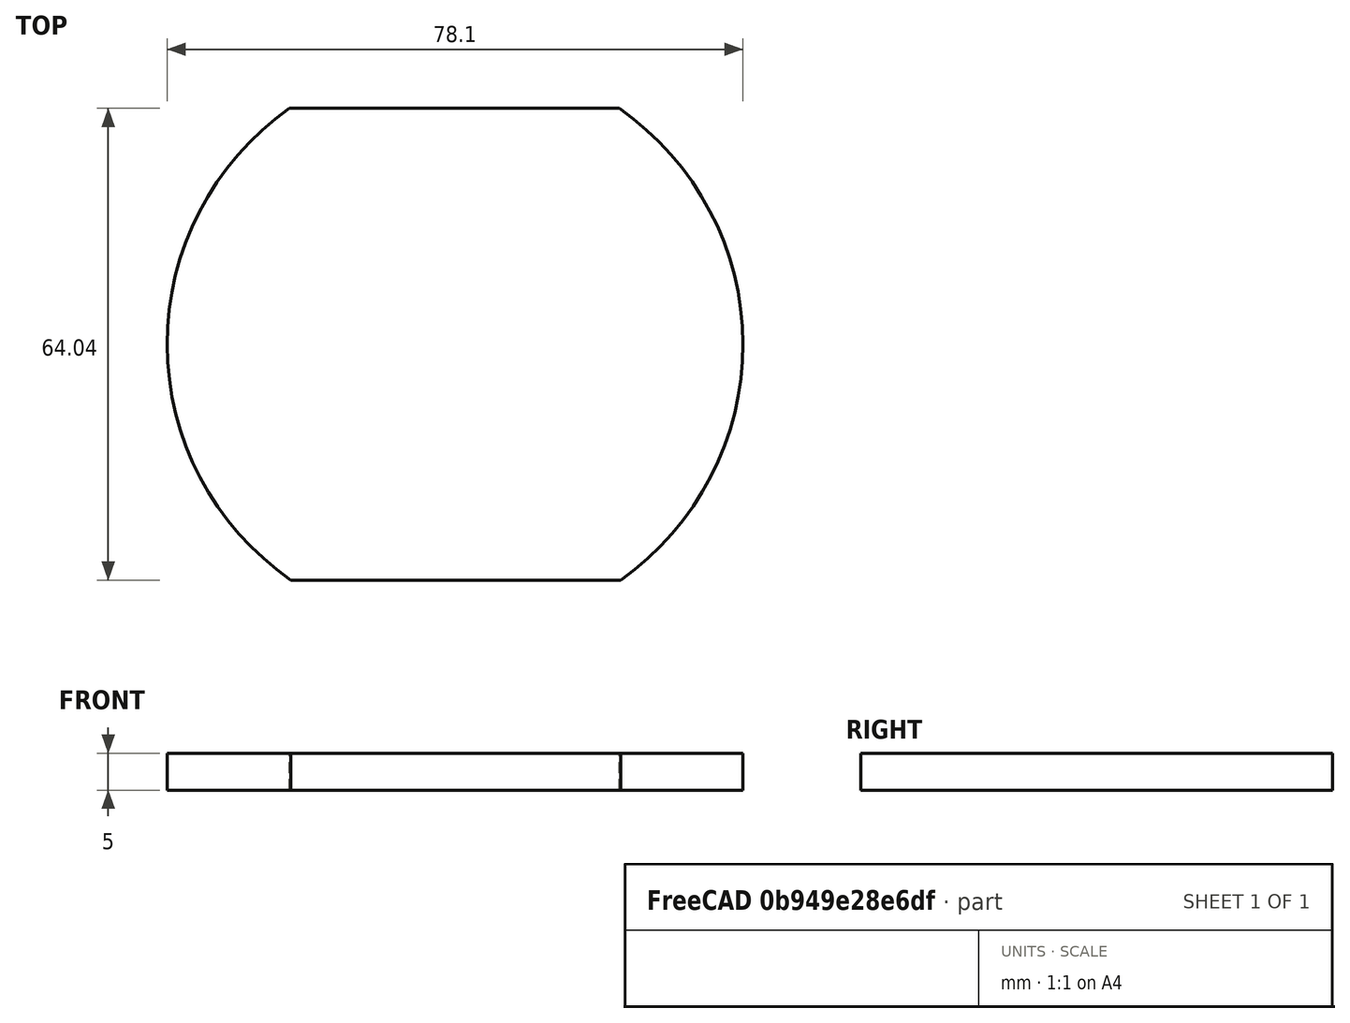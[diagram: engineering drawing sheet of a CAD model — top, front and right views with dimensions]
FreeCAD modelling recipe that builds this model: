
FCSTD DOCUMENT  (FreeCAD 1.0R39319 (Git))
Label: chapa_circle_90mm
License: All rights reserved
LicenseURL: https://en.wikipedia.org/wiki/All_rights_reserved
objects: Sketcher::SketchObject×1, PartDesign::Pad×1, PartDesign::Body×1
note: 6 computed .brp shape members not serialized (recipe doc carries the construction recipe); baked Part::Feature solids carry a one-line shape summary decoded from their .brp

FEATURE [Sketcher::SketchObject] Sketch_1
  ArcFitTolerance = 1e-06
  AttachmentSupport = -> [XY_Plane]
  FullyConstrained = false
  MakeInternals = false
  MapMode = 5
  sketch-geometry (4):
    g0: ArcOfCircle CenterX=-0.00136667 CenterY=0.11307 CenterZ=0 NormalX=0 NormalY=0 NormalZ=1 AngleXU=0 Radius=39.0546 StartAngle=5.32483 EndAngle=7.2474
    g1: LineSegment StartX=22.2621 StartY=32.2005 StartZ=0 EndX=-22.4507 EndY=32.2005 EndZ=0
    g2: ArcOfCircle CenterX=0.00214901 CenterY=0.244508 CenterZ=0 NormalX=0 NormalY=0 NormalZ=1 AngleXU=0 Radius=39.0553 StartAngle=2.18328 EndAngle=4.1058
    g3: LineSegment StartX=-22.2621 StartY=-31.8432 StartZ=0 EndX=22.4499 EndY=-31.8432 EndZ=0
  constraints (7):
    c: Coincident(g0,g1)
    c: Coincident(g1,g2)
    c: Coincident(g2,g3)
    c: Coincident(g3,g0)
    c: Parallel(g1,g3)
    c: Horizontal(g1)
    c: Distance(g1,g3) = 78
FEATURE [PartDesign::Pad] Pad_1
  Direction = (0,0,1)
  Length = 5
  Length2 = 10
  Profile = -> Sketch_1
  Refine = true
  Suppressed = false
  Type = 0
FEATURE [PartDesign::Body] Body
  AllowCompound = false
  Group = -> [Sketch_1,Pad_1]
  Origin = -> Origin
  Tip = -> Pad_1
